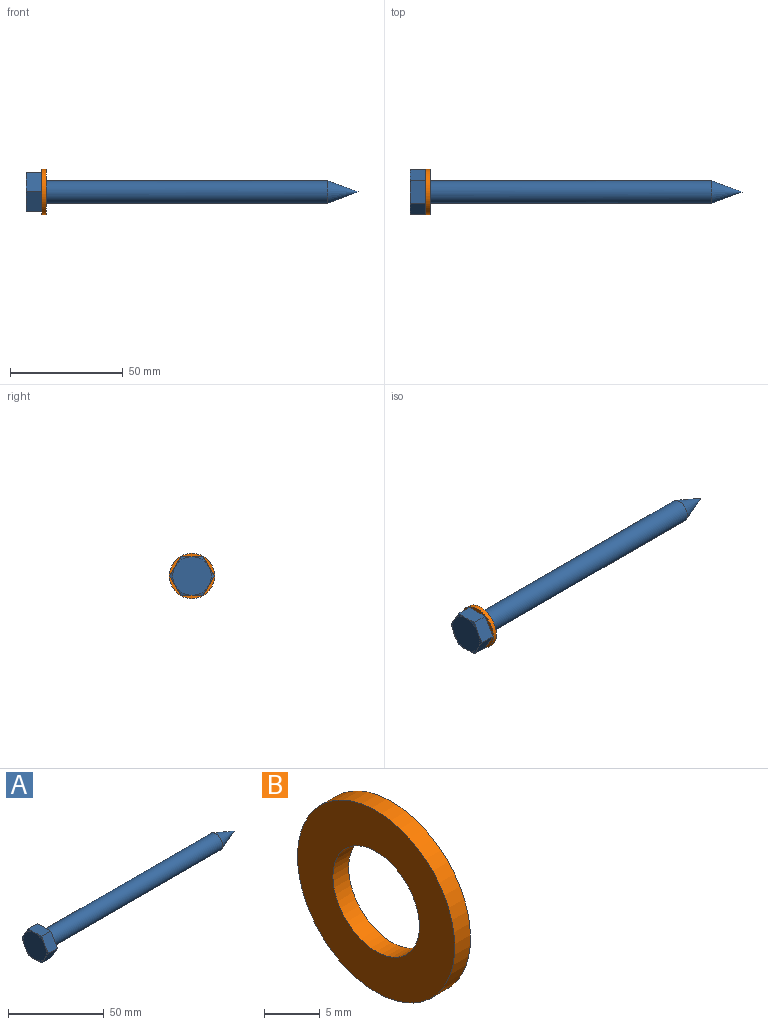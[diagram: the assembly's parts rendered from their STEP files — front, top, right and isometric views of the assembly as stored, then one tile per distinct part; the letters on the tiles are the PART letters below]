
ASSEMBLY  parts=2 mates=1
PART A: 17 faces, bbox 147.7x20.4x20.4 mm
  f0: plane 19.63x17mm, normal (1,0,0), area 133.4mm2, adj f1,f2,f3,f4,f5,f6,f14
  f1: plane 10.55x7.73mm, normal (0,0,1), area 67.5mm2, adj f0,f2,f6,f9,f10
  f2: plane 9.23x7.73mm, normal (0,0.87,0.5), area 67.5mm2, adj f0,f1,f3,f8,f9
  f3: plane 9.23x7.73mm, normal (0,0.87,-0.5), area 67.5mm2, adj f0,f2,f4,f7,f8
  f4: plane 10.55x7.73mm, normal (0,0,-1), area 67.5mm2, adj f0,f3,f5,f7,f12
  f5: plane 9.23x7.73mm, normal (0,-0.87,-0.5), area 67.5mm2, adj f0,f4,f6,f11,f12
  f6: plane 9.23x7.73mm, normal (0,-0.87,0.5), area 67.5mm2, adj f0,f1,f5,f10,f11
  f7: cone r=8.5mm half-angle=75deg, axis (1,0,0), area 6.4mm2, adj f3,f4,f13
  f8: cone r=8.5mm half-angle=75deg, axis (1,0,0), area 6.4mm2, adj f2,f3,f13
  f9: cone r=8.5mm half-angle=75deg, axis (1,0,0), area 6.4mm2, adj f1,f2,f13
  f10: cone r=8.5mm half-angle=75deg, axis (1,0,0), area 6.4mm2, adj f1,f6,f13
  f11: cone r=8.5mm half-angle=75deg, axis (1,0,0), area 6.4mm2, adj f5,f6,f13
  f12: cone r=8.5mm half-angle=75deg, axis (1,0,0), area 6.4mm2, adj f4,f5,f13
  f13: plane 17x17mm, normal (-1,0,0), area 227mm2, adj f7,f8,f9,f10,f11,f12
  f14: torus R=6.1mm, axis (1,0,0), area 58.6mm2, adj f0,f16
  f15: cone r=5mm half-angle=20.3deg, axis (-1,0,0), area 226.1mm2, adj f16
  f16: cylinder r=5mm len=125.4mm, axis (1,0,0), area 3939.6mm2, adj f14,f15
PART B: 4 faces, bbox 2x20x20 mm
  f0: plane 20x20mm, normal (-1,0,0), area 219.1mm2, adj f1,f3
  f1: cylinder r=5.5mm len=11mm, axis (1,0,0), area 69.1mm2, adj f0,f2
  f2: plane 20x20mm, normal (1,0,0), area 219.1mm2, adj f1,f3
  f3: cylinder r=10mm len=20mm, axis (1,0,0), area 125.7mm2, adj f0,f2
PLACE A at identity fixed
PLACE B at identity
MATE fastened A.f14 <-> B.f1  axis (1,0,0) through (0,0,0)mm
